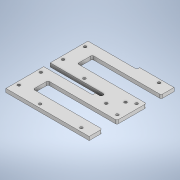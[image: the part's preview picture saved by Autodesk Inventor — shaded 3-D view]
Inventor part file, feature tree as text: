
AUTODESK INVENTOR PART (.ipt)
format: ipt  version: 2021 (Build 250183000, 183)  size: 233,472 bytes
history: native  units: mm
features: sketch x4, extrude x2, hole x2, projected_geometry x1
ambient origin geometry x8: Origin, YZ Plane, XZ Plane, XY Plane, X Axis, Y Axis, Z Axis, Center Point
bodies: Solid1 (feature_tree)
feature tree (9):
  extrude  "Extrusion1"  Depth=2.0mm
  sketch  "Sketch3"  dims[d11=2.0mm d12=5.0mm d13=0.0mm]
  hole  "Hole1"  [1 undecoded]
  extrude  "Extrusion2"  Depth=2.0mm
  hole  "Hole2"  [1 undecoded]
  sketch  "Sketch1"  dims[d3=20.75mm d4=2.0mm]
  sketch  "Sketch4"  dims[d26=2.0mm d27=59.25mm]
  projected_geometry  "Projected Loop1"
  sketch  "Sketch5"  dims[d28=59.25mm d29=116.2mm d30=20.0mm d31=5.1mm d32=2.55mm d33=40.0mm d34=18.0mm d35=5.0mm d36=5.0mm d37=7.5mm d38=13.0mm d39=15.5mm d40=15.5mm d41=13.0mm d42=7.5mm d43=16.0mm d44=12.0mm d45=73.5mm d46=3.8mm d47=6.0mm d48=4.0mm d49=2.0mm d50=90.0deg d51=8.0mm d52=20.594885mm d53=73.5mm d54=5.0mm d55=48.0mm d57=6.5mm d58=13.0mm d61=5.0mm d62=0.0mm d64=4.0mm d66=6.5mm d67=13.5mm d68=13.5mm d69=3.8mm d70=6.0mm d71=4.0mm d72=2.0mm d73=90.0deg d74=8.0mm d75=20.594885mm]
note: 2 required parameter values undecoded (feature->parameter linkage not recoverable at this tier; creation-order binding heuristic only, values carry confidence <= 0.55)
